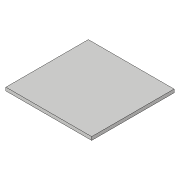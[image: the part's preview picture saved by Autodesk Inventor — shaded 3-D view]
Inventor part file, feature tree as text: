
AUTODESK INVENTOR PART (.ipt)
format: ipt  version: 2018.3 (Build 223284000, 284)  size: 73,216 bytes
history: native  units: in
note: dims shown in document units (in); Inventor stores cm internally (conversion verified against a paired STEP export)
features: extrude x1, sketch x1
ambient origin geometry x8: Origin, YZ Plane, XZ Plane, XY Plane, X Axis, Y Axis, Z Axis, Center Point
bodies: Solid1 (feature_tree)
feature tree (2):
  extrude  "Extrusion1"  Depth=3.125in
  sketch  "Sketch1"  dims[d0=3.25in d1=3.125in d2=0.125in d3=0.0in]
